FCSTD DOCUMENT  (FreeCAD 0.21R33668 +26 (Git))
Label: plan cuisine 2
License: All rights reserved
LicenseURL: http://en.wikipedia.org/wiki/All_rights_reserved
objects: Part::Part2DObjectPython×6, App::DocumentObjectGroup×1
note: 6 computed .brp shape members not serialized (recipe doc carries the construction recipe); baked Part::Feature solids carry a one-line shape summary decoded from their .brp

FEATURE [Part::Part2DObjectPython] Rectangle001  # Draft 2D object (typed FeaturePython)
  Area = 1.4e+07
  ChamferSize = 0
  Columns = 1
  FilletRadius = 0
  Height = 3500
  Length = 4000
  MakeFace = true
  Placement = pos=(157.351,123.815,0) rot=(0,0,1;0rad)
  Rows = 1
FEATURE [Part::Part2DObjectPython] Line001  # Draft 2D object (typed FeaturePython)
  Area = 0
  ChamferSize = 0
  Closed = false
  End = (755.9,1203.53,2.84e-14)
  FilletRadius = 0
  Length = 1302.49
  MakeFace = true
  Placement = pos=(-531.233,1190.64,199.01) rot=(0.819854,0.571939,-0.026929;0.154185rad)
  Points = (2) [(0,0,0),(1299.68,0.251328,-85.5577)]
  Start = (-531.233,1190.64,199.01)
  Subdivisions = 0
FEATURE [Part::Part2DObjectPython] Line002  # Draft 2D object (typed FeaturePython)
  Area = 0
  ChamferSize = 0
  Closed = false
  End = (3314.2,1945.46,-2.84e-14)
  FilletRadius = 0
  Length = 1299.88
  MakeFace = true
  Placement = pos=(4603.91,1931.08,-161.603) rot=(0.819854,0.571939,-0.026929;0.154185rad)
  Points = (2) [(0,0,0),(-1298.92,22.0716,44.9297)]
  Start = (4603.91,1931.08,-161.603)
  Subdivisions = 0
FEATURE [Part::Part2DObjectPython] Line003  # Draft 2D object (typed FeaturePython)
  Area = 0
  ChamferSize = 0
  Closed = false
  End = (3201.49,1321.15,2.274e-13)
  FilletRadius = 0
  Length = 1562.1
  MakeFace = true
  Placement = pos=(4268.93,1293.42,-1140.16) rot=(-0.084813,0.996181,-0.020739;0.255787rad)
  Points = (2) [(0,0,0),(-1320.48,-0.181013,834.552)]
  Start = (4268.93,1293.42,-1140.16)
  Subdivisions = 0
FEATURE [Part::Part2DObjectPython] Line  # Draft 2D object (typed FeaturePython)
  Area = 0
  ChamferSize = 0
  Closed = false
  End = (752.474,2198.59,0)
  FilletRadius = 0
  Length = 1577.47
  MakeFace = true
  Placement = pos=(-825,2198.46,0) rot=(0,0,1;0rad)
  Points = (2) [(0,0,0),(1577.47,0.122689,0)]
  Start = (-825,2198.46,0)
  Subdivisions = 0
FEATURE [Part::Part2DObjectPython] Rectangle  # Draft 2D object (typed FeaturePython)
  Area = 1.66762e+07
  ChamferSize = 0
  Columns = 1
  FilletRadius = 0
  Height = 3841.3
  Length = 4341.3
  MakeFace = true
  Placement = pos=(-13.2978,-46.8341,0) rot=(0,0,1;0rad)
  Rows = 1
FEATURE [App::DocumentObjectGroup] Draft_Construction  label="Construction"
  Group = -> [Rectangle001,Rectangle,Line002,Line003,Line]
